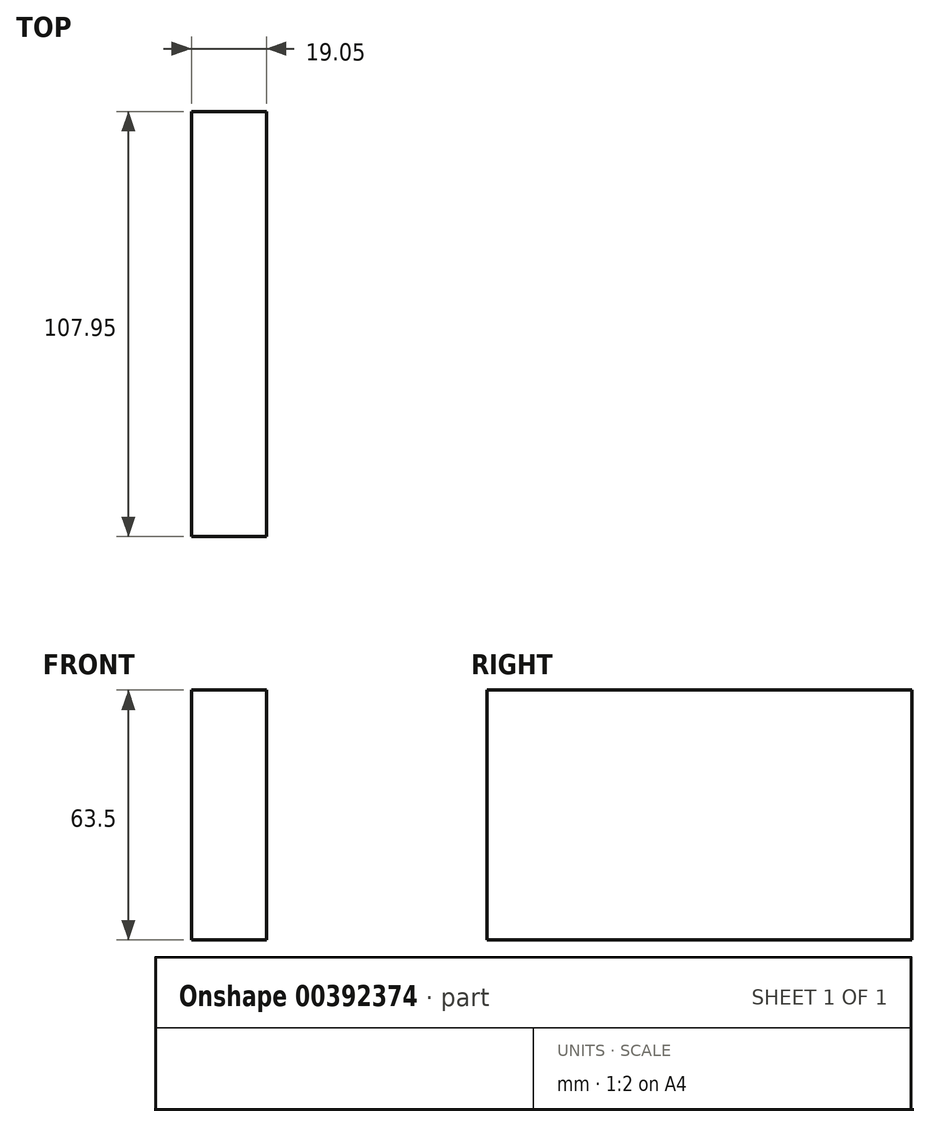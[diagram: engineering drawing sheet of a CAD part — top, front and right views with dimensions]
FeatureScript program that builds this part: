
annotation { "Feature Type Name" : "Feature", "Feature Type Description" : "" }
export const myFeature = defineFeature(function(context is Context, id is Id, definition is map)
    precondition{}
    {
        {
            var Q0;
            Q0=qCreatedBy(makeId("Right.planeOp"),FACE);
            var sketch = newSketch(context, id + "F0", { "sketchPlane" : qUnion([Q0])});
            skLineSegment(sketch, "E0.bottom", {"start": v(0, 0) * mm, "end": v(-107.95, 0) * mm});
            skLineSegment(sketch, "E0.top", {"start": v(0, -63.5) * mm, "end": v(-107.95, -63.5) * mm});
            skLineSegment(sketch, "E0.left", {"start": v(0, 0) * mm, "end": v(0, -63.5) * mm});
            skLineSegment(sketch, "E0.right", {"start": v(-107.95, 0) * mm, "end": v(-107.95, -63.5) * mm});
            skSolve(sketch);
        }
        {
            var Q0;
            Q0=makeQuery(id+"F0.imprint","IMPRINT",FACE,{"disambiguationData":[TD([[makeQuery(id+"F0.imprint","IMPRINT",EDGE,{"derivedFrom":sQuery(id+"F0.wireOp",EDGE,"E0.bottom")}),1.0]])]});
            extrude(context, id + "F1", {"entities" : qUnion([Q0]), "depth" : 19.05 * mm});
        }
    });
